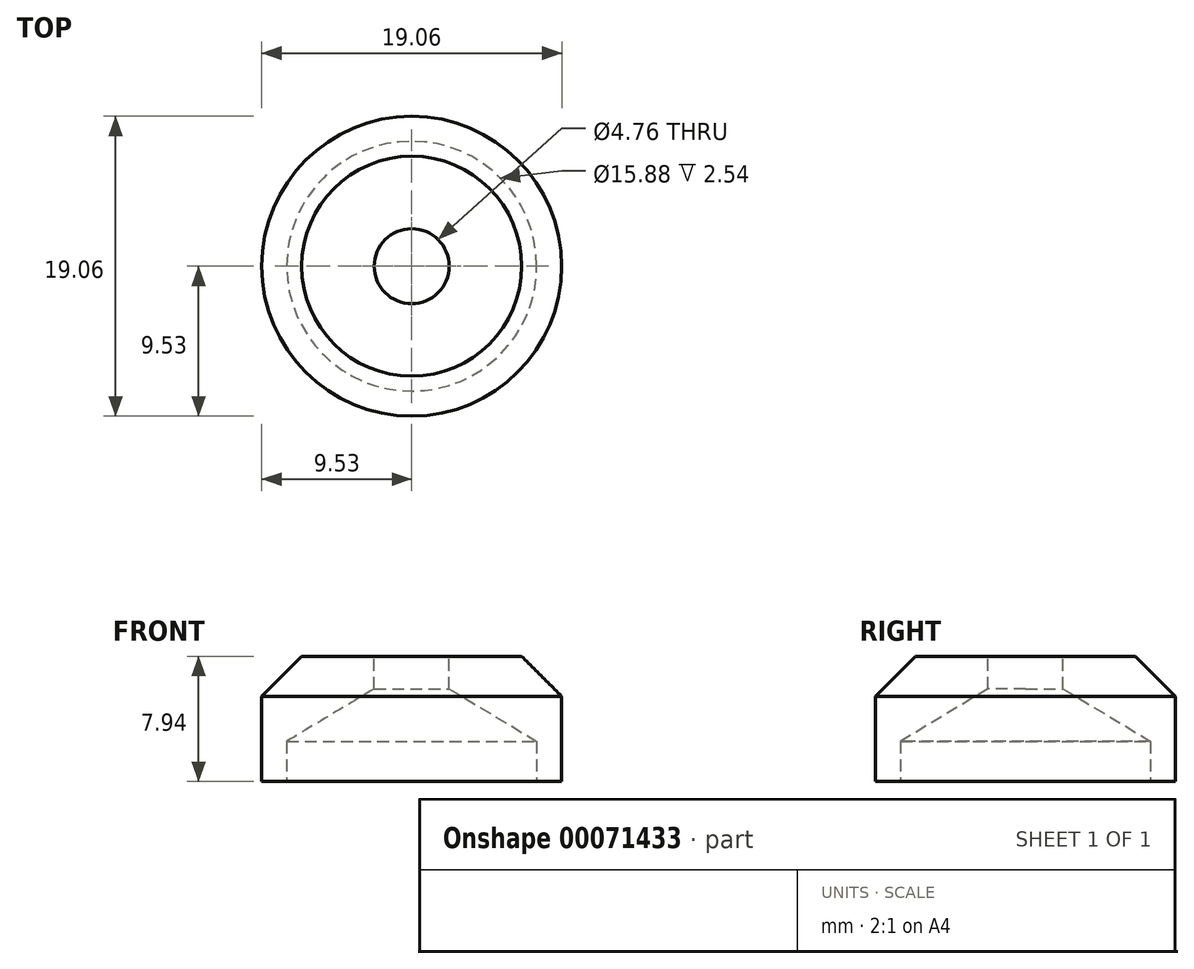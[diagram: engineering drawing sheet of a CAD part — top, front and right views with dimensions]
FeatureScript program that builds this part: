
annotation { "Feature Type Name" : "Feature", "Feature Type Description" : "" }
export const myFeature = defineFeature(function(context is Context, id is Id, definition is map)
    precondition{}
    {
        {
            var Q0;
            Q0=qCreatedBy(makeId("Top.planeOp"),FACE);
            var sketch = newSketch(context, id + "F0", { "sketchPlane" : qUnion([Q0])});
            skCircle(sketch, "E0", {"center": v(0, 0) * mm, "radius": 9.53 * mm});
            skSolve(sketch);
        }
        {
            var Q0;
            Q0=makeQuery(id+"F0.imprint","IMPRINT",FACE,{"disambiguationData":[TD([[makeQuery(id+"F0.imprint","IMPRINT",EDGE,{"derivedFrom":sQuery(id+"F0.wireOp",EDGE,"E0")}),1.0]])]});
            extrude(context, id + "F1", {"entities" : qUnion([Q0]), "depth" : 7.94 * mm});
        }
        {
            var Q0;
            Q0=makeQuery(id+"F1.opExtrude","CAP_EDGE",EDGE,{"disambiguationData":[OSD([sQuery(id+"F0.wireOp",EDGE,"E0")])],"isStart":false});
            chamfer(context, id + "F2", {"entities" : qUnion([Q0]), "chamferType" : ChamferType.TWO_OFFSETS, "width1" : 2.54 * mm, "oppositeDirection" : false, "width2" : 2.54 * mm, "tangentPropagation" : true});
        }
        {
            var Q0;
            Q0=makeQuery(id+"F1.opExtrude","CAP_FACE",FACE,{"disambiguationData":[OSD([sQuery(id+"F0.wireOp",EDGE,"E0")])],"isStart":false});
            var sketch = newSketch(context, id + "F3", { "sketchPlane" : qUnion([Q0])});
            skPoint(sketch, "E1", {"position": v(0, 0) * mm});
            skSolve(sketch);
        }
        {
            var Q0;
            Q0=sQuery(id+"F3.wireOp",VERTEX,"E1");
            var Q1;
            Q1=makeQuery(id+"F1.opExtrude","SWEPT_BODY",BODY,{"disambiguationData":[OSD([sQuery(id+"F0.wireOp",EDGE,"E0")])]});
            hole(context, id + "F4", {"style" : HoleStyle.SIMPLE, "holeDiameter" : 4.76 * mm, "endStyle" : HoleEndStyle.THROUGH, "locations" : qUnion([Q0]), "scope" : qUnion([Q1])});
        }
        {
            var Q0;
            Q0=makeQuery(id+"F1.opExtrude","CAP_FACE",FACE,{"disambiguationData":[OSD([sQuery(id+"F0.wireOp",EDGE,"E0")])],"isStart":true});
            var sketch = newSketch(context, id + "F5", { "sketchPlane" : qUnion([Q0])});
            skPoint(sketch, "E2", {"position": v(0, 0) * mm});
            skSolve(sketch);
        }
        {
            var Q0;
            Q0=sQuery(id+"F5.wireOp",VERTEX,"E2");
            var Q1;
            Q1=makeQuery(id+"F1.opExtrude","SWEPT_BODY",BODY,{"disambiguationData":[OSD([sQuery(id+"F0.wireOp",EDGE,"E0")])]});
            hole(context, id + "F6", {"style" : HoleStyle.SIMPLE, "holeDiameter" : 15.88 * mm, "endStyle" : HoleEndStyle.BLIND, "holeDepth" : 2.54 * mm, "locations" : qUnion([Q0]), "scope" : qUnion([Q1])});
        }
    });
